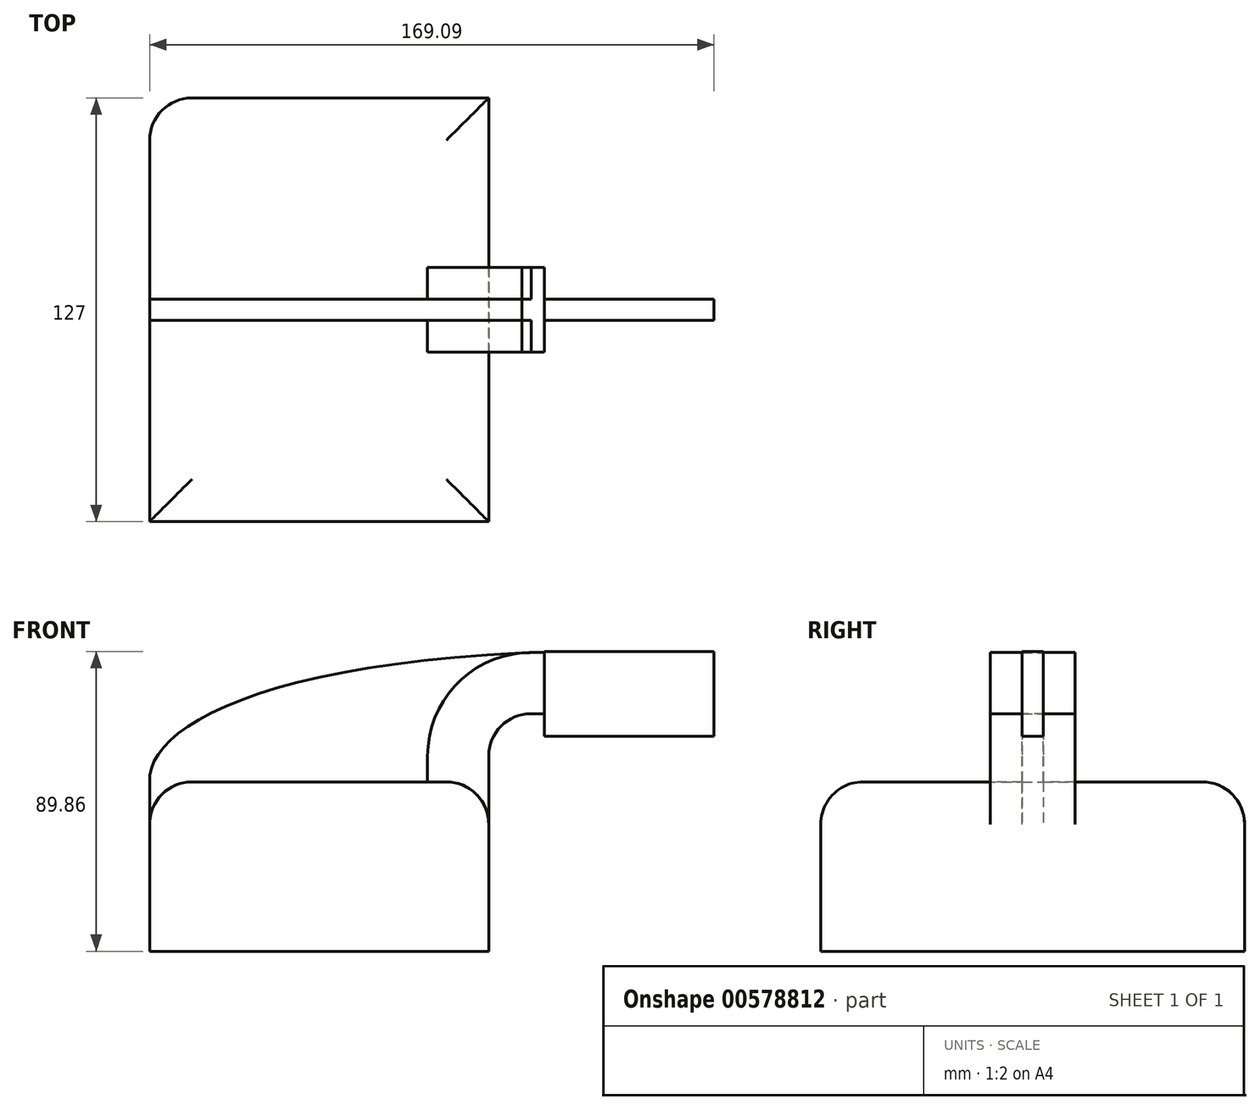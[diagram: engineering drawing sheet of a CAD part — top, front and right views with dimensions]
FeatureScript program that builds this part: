
annotation { "Feature Type Name" : "Feature", "Feature Type Description" : "" }
export const myFeature = defineFeature(function(context is Context, id is Id, definition is map)
    precondition{}
    {
        {
            var Q0;
            Q0=qCreatedBy(makeId("Front.planeOp"),FACE);
            var sketch = newSketch(context, id + "F0", { "sketchPlane" : qUnion([Q0])});
            skLineSegment(sketch, "E0.bottom", {"start": v(-50.8, 25.4) * mm, "end": v(50.8, 25.4) * mm});
            skLineSegment(sketch, "E0.top", {"start": v(-50.8, -25.4) * mm, "end": v(50.8, -25.4) * mm});
            skLineSegment(sketch, "E0.left", {"start": v(-50.8, 25.4) * mm, "end": v(-50.8, -25.4) * mm});
            skLineSegment(sketch, "E0.right", {"start": v(50.8, 25.4) * mm, "end": v(50.8, -25.4) * mm});
            skPoint(sketch, "E0.middle", {"position": v(0, 0) * mm});
            skLineSegment(sketch, "E1.bottom", {"start": v(67.48, 64.46) * mm, "end": v(118.28, 64.46) * mm});
            skLineSegment(sketch, "E1.top", {"start": v(67.48, 39.06) * mm, "end": v(118.28, 39.06) * mm});
            skLineSegment(sketch, "E1.left", {"start": v(67.48, 64.46) * mm, "end": v(67.48, 39.06) * mm});
            skLineSegment(sketch, "E1.right", {"start": v(118.28, 64.46) * mm, "end": v(118.28, 39.06) * mm});
            skPoint(sketch, "E1.middle", {"position": v(92.88, 51.76) * mm});
            skLineSegment(sketch, "E2", {"start": v(50.8, 25.4) * mm, "end": v(50.8, 33.14) * mm});
            skArc(sketch, "E3", {"start": v(50.8, 33.14) * mm, "mid": v(54.52, 42.12) * mm, "end": v(63.5, 45.84) * mm});
            skLineSegment(sketch, "E4", {"start": v(63.5, 45.84) * mm, "end": v(72.75, 45.84) * mm});
            skLineSegment(sketch, "E5.0", {"start": v(63.5, 64.15) * mm, "end": v(72.75, 64.15) * mm});
            skArc(sketch, "E5.1", {"start": v(32.49, 33.14) * mm, "mid": v(41.57, 55.07) * mm, "end": v(63.5, 64.15) * mm});
            skLineSegment(sketch, "E5.2", {"start": v(32.49, 25.4) * mm, "end": v(32.49, 33.14) * mm});
            skFitSpline(sketch, "E6", {"points": [v(-50.8, 25.4) * mm, v(63.5, 64.15) * mm], "startDerivative": vector(-2.27, 46.18) * mm, "endDerivative": vector(250.77, 10.63) * mm});
            skSolve(sketch);
        }
        {
            var Q0;
            Q0=makeQuery(id+"F0.imprint","IMPRINT",FACE,{"disambiguationData":[TD([[makeQuery(id+"F0.imprint","IMPRINT",EDGE,{"derivedFrom":sQuery(id+"F0.wireOp",EDGE,"E0.top")}),1.0]])]});
            extrude(context, id + "F1", {"entities" : qUnion([Q0]), "endBound" : BoundingType.SYMMETRIC, "depth" : 127 * mm, "offsetDistance" : 25.4 * mm});
        }
        {
            var Q0;
            {var subQ1=sQuery(id+"F0.wireOp",EDGE,"E2");Q0=makeQuery(id+"F0.imprint","IMPRINT",FACE,{"disambiguationData":[TD([[makeQuery(id+"F0.imprint","IMPRINT",EDGE,{"derivedFrom":subQ1}),1.0]])]});}
            extrude(context, id + "F2", {"entities" : qUnion([Q0]), "operationType" : NewBodyOperationType.ADD, "endBound" : BoundingType.SYMMETRIC, "oppositeDirection" : true, "depth" : 25.4 * mm, "offsetDistance" : 25.4 * mm});
        }
        {
            var Q0;
            Q0 = qSketchRegion(id + "F0", true);
            extrude(context, id + "F3", {"entities" : qUnion([Q0]), "operationType" : NewBodyOperationType.ADD, "endBound" : BoundingType.SYMMETRIC, "depth" : 6.35 * mm, "offsetDistance" : 25.4 * mm});
        }
        {
            var Q0;
            {var subQ0=sQuery(id+"F0.wireOp",EDGE,"E6");var subQ1=sQuery(id+"F0.wireOp",EDGE,"E0.right");var subQ2=sQuery(id+"F0.wireOp",EDGE,"E0.left");var subQ3=sQuery(id+"F0.wireOp",EDGE,"E0.top");var subQ4=sQuery(id+"F0.wireOp",EDGE,"E0.bottom");Q0=makeQuery(id+"F3.boolean.opBoolean","SPLIT",EDGE,{"disambiguationData":[TD([makeQuery(id+"F1.opExtrude","CAP_FACE",FACE,{"disambiguationData":[OSD([subQ4,subQ3,subQ2,subQ1])],"isStart":true})])],"derivedFrom":makeQuery(id+"F1.opExtrude","SWEPT_EDGE",EDGE,{"disambiguationData":[OSD([subQ4,subQ2,subQ0])]})});}
            var Q1;
            Q1=makeQuery(id+"F1.opExtrude","CAP_EDGE",EDGE,{"disambiguationData":[OSD([sQuery(id+"F0.wireOp",EDGE,"E0.bottom")])],"isStart":true});
            var Q2;
            {var subQ0=sQuery(id+"F0.wireOp",EDGE,"E2");var subQ1=sQuery(id+"F0.wireOp",EDGE,"E0.bottom");var subQ2=sQuery(id+"F0.wireOp",EDGE,"E0.right");Q2=makeQuery(id+"F2.boolean.opBoolean","SPLIT",EDGE,{"disambiguationData":[TD([makeQuery(id+"F1.opExtrude","CAP_FACE",FACE,{"disambiguationData":[OSD([subQ1,sQuery(id+"F0.wireOp",EDGE,"E0.top"),sQuery(id+"F0.wireOp",EDGE,"E0.left"),subQ2])],"isStart":true})])],"derivedFrom":makeQuery(id+"F1.opExtrude","SWEPT_EDGE",EDGE,{"disambiguationData":[OSD([subQ1,subQ2,subQ0])]})});}
            var Q3;
            Q3=makeQuery(id+"F1.opExtrude","CAP_EDGE",EDGE,{"disambiguationData":[OSD([sQuery(id+"F0.wireOp",EDGE,"E0.bottom")])],"isStart":false});
            var Q4;
            {var subQ0=sQuery(id+"F0.wireOp",EDGE,"E2");var subQ1=sQuery(id+"F0.wireOp",EDGE,"E0.bottom");var subQ2=sQuery(id+"F0.wireOp",EDGE,"E0.right");Q4=makeQuery(id+"F2.boolean.opBoolean","SPLIT",EDGE,{"disambiguationData":[TD([makeQuery(id+"F1.opExtrude","CAP_FACE",FACE,{"disambiguationData":[OSD([subQ1,sQuery(id+"F0.wireOp",EDGE,"E0.top"),sQuery(id+"F0.wireOp",EDGE,"E0.left"),subQ2])],"isStart":false})])],"derivedFrom":makeQuery(id+"F1.opExtrude","SWEPT_EDGE",EDGE,{"disambiguationData":[OSD([subQ1,subQ2,subQ0])]})});}
            var Q5;
            {var subQ0=sQuery(id+"F0.wireOp",EDGE,"E0.left");var subQ1=sQuery(id+"F0.wireOp",EDGE,"E6");var subQ2=sQuery(id+"F0.wireOp",EDGE,"E0.right");var subQ3=sQuery(id+"F0.wireOp",EDGE,"E0.top");var subQ4=sQuery(id+"F0.wireOp",EDGE,"E0.bottom");Q5=makeQuery(id+"F3.boolean.opBoolean","SPLIT",EDGE,{"disambiguationData":[TD([makeQuery(id+"F1.opExtrude","CAP_FACE",FACE,{"disambiguationData":[OSD([subQ4,subQ3,subQ0,subQ2])],"isStart":false})])],"derivedFrom":makeQuery(id+"F1.opExtrude","SWEPT_EDGE",EDGE,{"disambiguationData":[OSD([subQ4,subQ0,subQ1])]})});}
            var Q6;
            Q6=makeQuery(id+"F1.opExtrude","CAP_EDGE",EDGE,{"disambiguationData":[OSD([sQuery(id+"F0.wireOp",EDGE,"E0.left")])],"isStart":true});
            fillet(context, id + "F4", {"entities" : qUnion([Q0, Q1, Q2, Q3, Q4, Q5, Q6]), "radius" : 12.7 * mm, "tangentPropagation" : true, "allowEdgeOverflow" : false});
        }
    });
